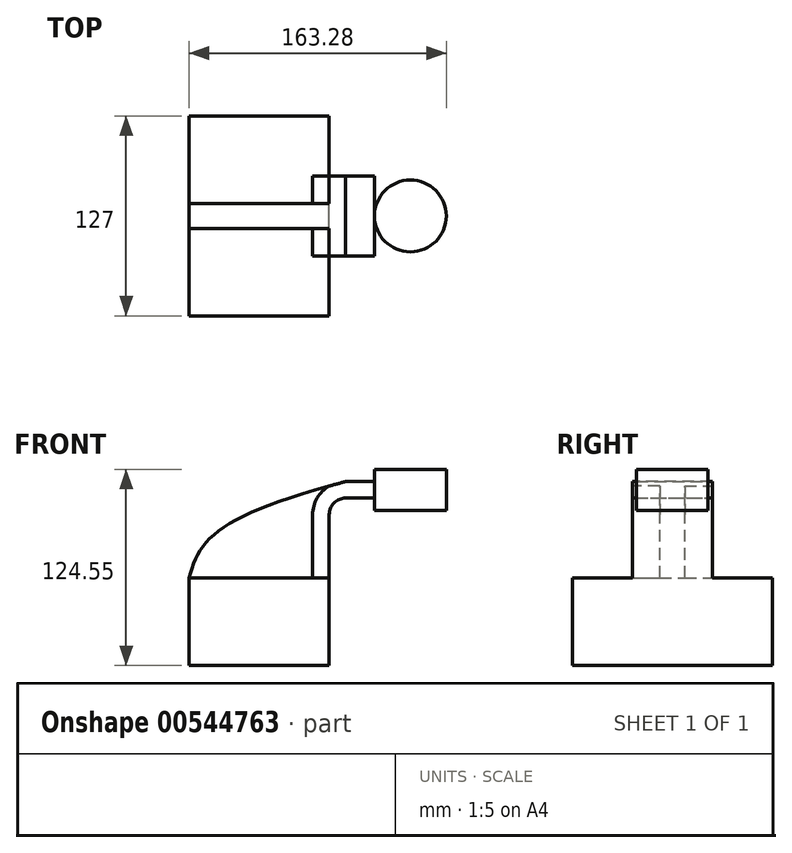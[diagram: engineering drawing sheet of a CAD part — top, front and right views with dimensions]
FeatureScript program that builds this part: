
annotation { "Feature Type Name" : "Feature", "Feature Type Description" : "" }
export const myFeature = defineFeature(function(context is Context, id is Id, definition is map)
    precondition{}
    {
        {
            var Q0;
            Q0=qCreatedBy(makeId("Front.planeOp"),FACE);
            var sketch = newSketch(context, id + "F0", { "sketchPlane" : qUnion([Q0])});
            skLineSegment(sketch, "E0.bottom", {"start": v(-44.45, 27.83) * mm, "end": v(44.45, 27.83) * mm});
            skLineSegment(sketch, "E0.top", {"start": v(-44.45, -27.83) * mm, "end": v(44.45, -27.83) * mm});
            skLineSegment(sketch, "E0.left", {"start": v(-44.45, 27.83) * mm, "end": v(-44.45, -27.83) * mm});
            skLineSegment(sketch, "E0.right", {"start": v(44.45, 27.83) * mm, "end": v(44.45, -27.83) * mm});
            skPoint(sketch, "E0.middle", {"position": v(0, 0) * mm});
            skLineSegment(sketch, "E1.bottom", {"start": v(118.83, 70.8) * mm, "end": v(73.22, 70.8) * mm});
            skLineSegment(sketch, "E1.top", {"start": v(118.83, 96.72) * mm, "end": v(73.22, 96.72) * mm});
            skLineSegment(sketch, "E1.left", {"start": v(118.83, 70.8) * mm, "end": v(118.83, 96.72) * mm});
            skLineSegment(sketch, "E1.right", {"start": v(73.22, 70.8) * mm, "end": v(73.22, 96.72) * mm});
            skPoint(sketch, "E1.middle", {"position": v(96.03, 83.76) * mm});
            skLineSegment(sketch, "E2", {"start": v(44.45, 27.83) * mm, "end": v(44.45, 68.03) * mm});
            skArc(sketch, "E3", {"start": v(44.45, 68.03) * mm, "mid": v(47.52, 75.45) * mm, "end": v(54.94, 78.52) * mm});
            skLineSegment(sketch, "E4", {"start": v(54.94, 78.52) * mm, "end": v(96.03, 78.52) * mm});
            skLineSegment(sketch, "E5.0", {"start": v(54.94, 89) * mm, "end": v(96.03, 89) * mm});
            skArc(sketch, "E5.1", {"start": v(33.98, 68.03) * mm, "mid": v(40.12, 82.85) * mm, "end": v(54.94, 89) * mm});
            skLineSegment(sketch, "E5.2", {"start": v(33.98, 27.83) * mm, "end": v(33.98, 68.03) * mm});
            skLineSegment(sketch, "E6", {"start": v(96.03, 89) * mm, "end": v(96.03, 78.52) * mm});
            skFitSpline(sketch, "E7", {"points": [v(-44.45, 27.83) * mm, v(54.94, 89) * mm], "startDerivative": vector(18.8, 76.72) * mm, "endDerivative": vector(239.93, 63.27) * mm});
            skLineSegment(sketch, "E8", {"start": v(96.03, 96.72) * mm, "end": v(96.03, 70.8) * mm});
            skSolve(sketch);
        }
        {
            var Q0;
            Q0=makeQuery(id+"F0.imprint","IMPRINT",FACE,{"disambiguationData":[TD([[makeQuery(id+"F0.imprint","IMPRINT",EDGE,{"derivedFrom":sQuery(id+"F0.wireOp",EDGE,"E0.top")}),1.0]])]});
            extrude(context, id + "F1", {"entities" : qUnion([Q0]), "endBound" : BoundingType.SYMMETRIC, "depth" : 127 * mm, "offsetDistance" : 25.4 * mm});
        }
        {
            var Q0;
            {var subQ1=sQuery(id+"F0.wireOp",EDGE,"E2");Q0=makeQuery(id+"F0.imprint","IMPRINT",FACE,{"disambiguationData":[TD([[makeQuery(id+"F0.imprint","IMPRINT",EDGE,{"derivedFrom":subQ1}),1.0]])]});}
            extrude(context, id + "F2", {"entities" : qUnion([Q0]), "operationType" : NewBodyOperationType.ADD, "endBound" : BoundingType.SYMMETRIC, "depth" : 50.8 * mm, "offsetDistance" : 25.4 * mm});
        }
        {
            var Q0;
            {var subQ3=sQuery(id+"F0.wireOp",EDGE,"E5.2");Q0=makeQuery(id+"F0.imprint","IMPRINT",FACE,{"disambiguationData":[TD([[makeQuery(id+"F0.imprint","IMPRINT",EDGE,{"derivedFrom":subQ3}),1.0]])]});}
            extrude(context, id + "F3", {"entities" : qUnion([Q0]), "operationType" : NewBodyOperationType.ADD, "endBound" : BoundingType.SYMMETRIC, "depth" : 15.88 * mm, "offsetDistance" : 25.4 * mm});
        }
        {
            var Q0;
            {var subQ4=sQuery(id+"F0.wireOp",EDGE,"E1.left");Q0=makeQuery(id+"F0.imprint","IMPRINT",FACE,{"disambiguationData":[TD([[makeQuery(id+"F0.imprint","IMPRINT",EDGE,{"derivedFrom":subQ4}),1.0]])]});}
            var Q1;
            Q1=sQuery(id+"F0.wireOp",EDGE,"E8");
            revolve(context, id + "F4", {"operationType" : NewBodyOperationType.ADD, "entities" : qUnion([Q0]), "axis" : qUnion([Q1]), "revolveType" : RevolveType.FULL});
        }
    });
